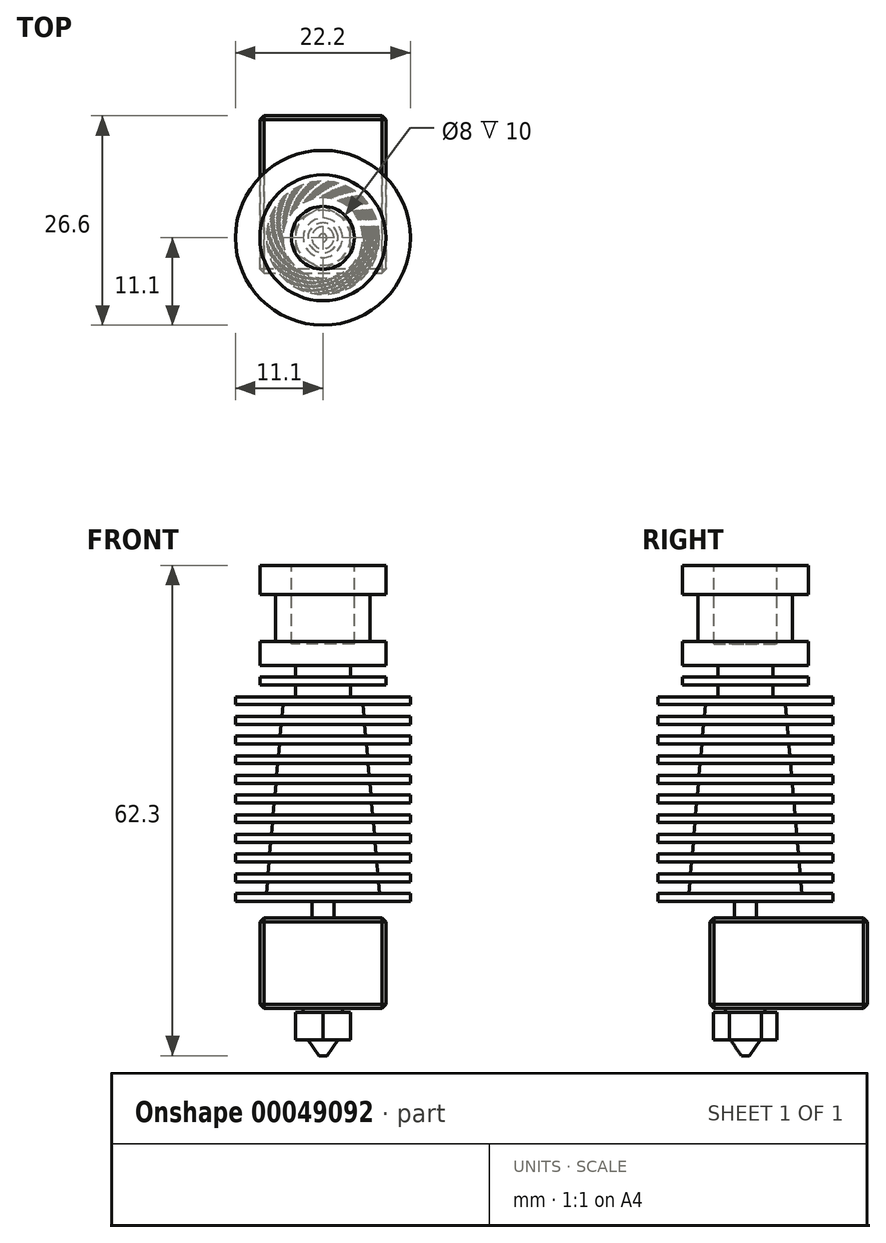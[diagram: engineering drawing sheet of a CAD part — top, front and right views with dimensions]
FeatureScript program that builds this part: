
annotation { "Feature Type Name" : "Feature", "Feature Type Description" : "" }
export const myFeature = defineFeature(function(context is Context, id is Id, definition is map)
    precondition{}
    {
        {
            var Q0;
            Q0=qCreatedBy(makeId("Front.planeOp"),FACE);
            var sketch = newSketch(context, id + "F0", { "sketchPlane" : qUnion([Q0])});
            skLineSegment(sketch, "E0", {"start": v(0, 42.7) * mm, "end": v(8, 42.7) * mm});
            skLineSegment(sketch, "E1", {"start": v(8, 42.7) * mm, "end": v(8, 39) * mm});
            skLineSegment(sketch, "E2", {"start": v(8, 39) * mm, "end": v(6, 39) * mm});
            skLineSegment(sketch, "E3", {"start": v(6, 39) * mm, "end": v(6, 33) * mm});
            skLineSegment(sketch, "E4", {"start": v(6, 33) * mm, "end": v(8, 33) * mm});
            skLineSegment(sketch, "E5", {"start": v(8, 33) * mm, "end": v(8, 30) * mm});
            skLineSegment(sketch, "E6", {"start": v(8, 30) * mm, "end": v(3.5, 30) * mm});
            skLineSegment(sketch, "E7", {"start": v(3.5, 30) * mm, "end": v(3.5, 28.5) * mm});
            skLineSegment(sketch, "E8", {"start": v(3.5, 28.5) * mm, "end": v(8, 28.5) * mm});
            skLineSegment(sketch, "E9", {"start": v(8, 28.5) * mm, "end": v(8, 27.5) * mm});
            skLineSegment(sketch, "E10", {"start": v(8, 27.5) * mm, "end": v(3.5, 27.5) * mm});
            skLineSegment(sketch, "E11", {"start": v(3.5, 27.5) * mm, "end": v(3.5, 26) * mm});
            skLineSegment(sketch, "E12", {"start": v(3.5, 26) * mm, "end": v(11.1, 26) * mm});
            skLineSegment(sketch, "E13", {"start": v(11.1, 26) * mm, "end": v(11.1, 0) * mm, "construction": true});
            skLineSegment(sketch, "E14", {"start": v(0, 0) * mm, "end": v(0, 42.7) * mm});
            skLineSegment(sketch, "E15", {"start": v(11.1, 0) * mm, "end": v(1.4, 0) * mm});
            skLineSegment(sketch, "E16", {"start": v(1.4, 0) * mm, "end": v(1.4, -2.1) * mm});
            skLineSegment(sketch, "E17", {"start": v(1.4, -2.1) * mm, "end": v(0, -2.1) * mm});
            skLineSegment(sketch, "E18", {"start": v(0, -2.1) * mm, "end": v(0, 0) * mm});
            skLineSegment(sketch, "E19", {"start": v(5, 26) * mm, "end": v(7.27, 0) * mm, "construction": true});
            skLineSegment(sketch, "E20", {"start": v(11.1, 26) * mm, "end": v(11.1, 25) * mm});
            skLineSegment(sketch, "E21", {"start": v(11.1, 25) * mm, "end": v(5.09, 25) * mm});
            skLineSegment(sketch, "E22", {"start": v(5.09, 25) * mm, "end": v(5.22, 23.5) * mm});
            skLineSegment(sketch, "E23", {"start": v(5.22, 23.5) * mm, "end": v(11.1, 23.5) * mm});
            skLineSegment(sketch, "E24", {"start": v(11.1, 23.5) * mm, "end": v(11.1, 22.5) * mm});
            skLineSegment(sketch, "E25", {"start": v(11.1, 22.5) * mm, "end": v(5.3, 22.5) * mm});
            skLineSegment(sketch, "E26", {"start": v(5.3, 22.5) * mm, "end": v(5.44, 21) * mm});
            skLineSegment(sketch, "E27", {"start": v(5.44, 21) * mm, "end": v(11.1, 21) * mm});
            skLineSegment(sketch, "E28", {"start": v(11.1, 21) * mm, "end": v(11.1, 20) * mm});
            skLineSegment(sketch, "E29", {"start": v(11.1, 20) * mm, "end": v(5.52, 20) * mm});
            skLineSegment(sketch, "E30", {"start": v(5.52, 20) * mm, "end": v(5.66, 18.5) * mm});
            skLineSegment(sketch, "E31", {"start": v(5.66, 18.5) * mm, "end": v(11.1, 18.5) * mm});
            skLineSegment(sketch, "E32", {"start": v(11.1, 18.5) * mm, "end": v(11.1, 17.5) * mm});
            skLineSegment(sketch, "E33", {"start": v(11.1, 17.5) * mm, "end": v(5.74, 17.5) * mm});
            skLineSegment(sketch, "E34", {"start": v(5.74, 17.5) * mm, "end": v(5.87, 16) * mm});
            skLineSegment(sketch, "E35", {"start": v(5.87, 16) * mm, "end": v(11.1, 16) * mm});
            skLineSegment(sketch, "E36", {"start": v(11.1, 16) * mm, "end": v(11.1, 15) * mm});
            skLineSegment(sketch, "E37", {"start": v(11.1, 15) * mm, "end": v(5.96, 15) * mm});
            skLineSegment(sketch, "E38", {"start": v(5.96, 15) * mm, "end": v(6.1, 13.5) * mm});
            skLineSegment(sketch, "E39", {"start": v(6.1, 13.5) * mm, "end": v(11.1, 13.5) * mm});
            skLineSegment(sketch, "E40", {"start": v(11.1, 13.5) * mm, "end": v(11.1, 12.5) * mm});
            skLineSegment(sketch, "E41", {"start": v(11.1, 12.5) * mm, "end": v(6.18, 12.5) * mm});
            skLineSegment(sketch, "E42", {"start": v(6.18, 12.5) * mm, "end": v(6.31, 11) * mm});
            skLineSegment(sketch, "E43", {"start": v(6.31, 11) * mm, "end": v(11.1, 11) * mm});
            skLineSegment(sketch, "E44", {"start": v(11.1, 11) * mm, "end": v(11.1, 10) * mm});
            skLineSegment(sketch, "E45", {"start": v(11.1, 10) * mm, "end": v(6.4, 10) * mm});
            skLineSegment(sketch, "E46", {"start": v(6.4, 10) * mm, "end": v(6.53, 8.5) * mm});
            skLineSegment(sketch, "E47", {"start": v(6.53, 8.5) * mm, "end": v(11.1, 8.5) * mm});
            skLineSegment(sketch, "E48", {"start": v(11.1, 8.5) * mm, "end": v(11.1, 7.5) * mm});
            skLineSegment(sketch, "E49", {"start": v(11.1, 7.5) * mm, "end": v(6.62, 7.5) * mm});
            skLineSegment(sketch, "E50", {"start": v(6.62, 7.5) * mm, "end": v(6.75, 6) * mm});
            skLineSegment(sketch, "E51", {"start": v(6.75, 6) * mm, "end": v(11.1, 6) * mm});
            skLineSegment(sketch, "E52", {"start": v(11.1, 6) * mm, "end": v(11.1, 5) * mm});
            skLineSegment(sketch, "E53", {"start": v(11.1, 5) * mm, "end": v(6.84, 5) * mm});
            skLineSegment(sketch, "E54", {"start": v(6.84, 5) * mm, "end": v(6.97, 3.5) * mm});
            skLineSegment(sketch, "E55", {"start": v(6.97, 3.5) * mm, "end": v(11.1, 3.5) * mm});
            skLineSegment(sketch, "E56", {"start": v(11.1, 3.5) * mm, "end": v(11.1, 2.5) * mm});
            skLineSegment(sketch, "E57", {"start": v(11.1, 2.5) * mm, "end": v(7.06, 2.5) * mm});
            skLineSegment(sketch, "E58", {"start": v(7.06, 2.5) * mm, "end": v(7.19, 1) * mm});
            skLineSegment(sketch, "E59", {"start": v(7.19, 1) * mm, "end": v(11.1, 1) * mm});
            skLineSegment(sketch, "E60", {"start": v(11.1, 1) * mm, "end": v(11.1, 0) * mm});
            skSolve(sketch);
        }
        {
            var Q0;
            Q0=makeQuery(id+"F0.imprint","IMPRINT",FACE,{"disambiguationData":[TD([[makeQuery(id+"F0.imprint","IMPRINT",EDGE,{"derivedFrom":sQuery(id+"F0.wireOp",EDGE,"E0")}),-1.0]])]});
            var Q1;
            Q1=sQuery(id+"F0.wireOp",EDGE,"E14");
            revolve(context, id + "F1", {"entities" : qUnion([Q0]), "axis" : qUnion([Q1]), "revolveType" : RevolveType.FULL});
        }
        {
            var Q0;
            Q0=makeQuery(id+"F1.opRevolve","SWEPT_FACE",FACE,{"disambiguationData":[OSD([sQuery(id+"F0.wireOp",EDGE,"E17")])]});
            var sketch = newSketch(context, id + "F2", { "sketchPlane" : qUnion([Q0])});
            skLineSegment(sketch, "E61.bottom", {"start": v(-15.5, 8) * mm, "end": v(4.5, 8) * mm});
            skLineSegment(sketch, "E61.top", {"start": v(-15.5, -8) * mm, "end": v(4.5, -8) * mm});
            skLineSegment(sketch, "E61.left", {"start": v(-15.5, 8) * mm, "end": v(-15.5, -8) * mm});
            skLineSegment(sketch, "E61.right", {"start": v(4.5, 8) * mm, "end": v(4.5, -8) * mm});
            skPoint(sketch, "E62.0", {"position": v(0, 0) * mm});
            skLineSegment(sketch, "E63", {"start": v(-15.5, 0) * mm, "end": v(4.5, 0) * mm, "construction": true});
            skSolve(sketch);
        }
        {
            var Q0;
            Q0=makeQuery(id+"F2.imprint","IMPRINT",FACE,{"disambiguationData":[TD([[makeQuery(id+"F2.imprint","IMPRINT",EDGE,{"derivedFrom":sQuery(id+"F2.wireOp",EDGE,"E61.bottom")}),-1.0]])]});
            var Q1;
            Q1=makeQuery(id+"F2.imprint","IMPRINT",FACE,{"disambiguationData":[TD([[makeQuery(id+"F2.imprint","IMPRINT",EDGE,{"derivedFrom":makeQuery(id+"F1.opRevolve","SWEPT_EDGE",EDGE,{"disambiguationData":[OSD([sQuery(id+"F0.wireOp",EDGE,"E16"),sQuery(id+"F0.wireOp",EDGE,"E17")])]})}),1.0]])]});
            extrude(context, id + "F3", {"entities" : qUnion([Q0, Q1]), "operationType" : NewBodyOperationType.ADD, "depth" : 11.5 * mm});
        }
        {
            var Q0;
            Q0=makeQuery(id+"F3.opExtrude","SWEPT_FACE",FACE,{"disambiguationData":[OSD([sQuery(id+"F2.wireOp",EDGE,"E61.bottom")])]});
            var Q1;
            Q1=makeQuery(id+"F3.opExtrude","SWEPT_FACE",FACE,{"disambiguationData":[OSD([sQuery(id+"F2.wireOp",EDGE,"E61.right")])]});
            var Q2;
            Q2=makeQuery(id+"F3.opExtrude","SWEPT_FACE",FACE,{"disambiguationData":[OSD([sQuery(id+"F2.wireOp",EDGE,"E61.top")])]});
            var Q3;
            Q3=makeQuery(id+"F3.opExtrude","SWEPT_FACE",FACE,{"disambiguationData":[OSD([sQuery(id+"F2.wireOp",EDGE,"E61.left")])]});
            chamfer(context, id + "F4", {"entities" : qUnion([Q0, Q1, Q2, Q3]), "width" : .5 * mm, "tangentPropagation" : true});
        }
        {
            var Q0;
            Q0=qCreatedBy(makeId("Front.planeOp"),FACE);
            var sketch = newSketch(context, id + "F5", { "sketchPlane" : qUnion([Q0])});
            skLineSegment(sketch, "E64", {"start": v(0, -7.1) * mm, "end": v(0, -19.6) * mm});
            skLineSegment(sketch, "E65", {"start": v(0, -19.6) * mm, "end": v(0.5, -19.6) * mm});
            skLineSegment(sketch, "E66", {"start": v(0.5, -19.6) * mm, "end": v(1.9, -17.6) * mm});
            skLineSegment(sketch, "E67", {"start": v(1.9, -17.6) * mm, "end": v(2.5, -17.6) * mm});
            skLineSegment(sketch, "E68", {"start": v(2.5, -17.6) * mm, "end": v(2.5, -14.6) * mm});
            skLineSegment(sketch, "E69", {"start": v(2.5, -14.6) * mm, "end": v(2.5, -7.1) * mm});
            skLineSegment(sketch, "E70", {"start": v(2.5, -7.1) * mm, "end": v(0, -7.1) * mm});
            skSolve(sketch);
        }
        {
            var Q0;
            Q0=makeQuery(id+"F5.imprint","IMPRINT",FACE,{"disambiguationData":[TD([[makeQuery(id+"F5.imprint","IMPRINT",EDGE,{"derivedFrom":sQuery(id+"F5.wireOp",EDGE,"E64")}),1.0]])]});
            var Q1;
            Q1=sQuery(id+"F5.wireOp",EDGE,"E64");
            revolve(context, id + "F6", {"operationType" : NewBodyOperationType.ADD, "entities" : qUnion([Q0]), "axis" : qUnion([Q1]), "revolveType" : RevolveType.FULL});
        }
        {
            var Q0;
            Q0=makeQuery(id+"F6.opRevolve","SWEPT_FACE",FACE,{"disambiguationData":[OSD([sQuery(id+"F5.wireOp",EDGE,"E67")])]});
            var sketch = newSketch(context, id + "F7", { "sketchPlane" : qUnion([Q0])});
            skCircle(sketch, "E71.cCircle", {"center": v(0, 0) * mm, "radius": 3.5 * mm, "construction": true});
            skLineSegment(sketch, "E71.0", {"start": v(4.04, 0) * mm, "end": v(2.02, -3.5) * mm});
            skLineSegment(sketch, "E71.1", {"start": v(2.02, -3.5) * mm, "end": v(-2.02, -3.5) * mm});
            skLineSegment(sketch, "E71.2", {"start": v(-2.02, -3.5) * mm, "end": v(-4.04, 0) * mm});
            skLineSegment(sketch, "E71.3", {"start": v(-4.04, 0) * mm, "end": v(-2.02, 3.5) * mm});
            skLineSegment(sketch, "E71.4", {"start": v(-2.02, 3.5) * mm, "end": v(2.02, 3.5) * mm});
            skLineSegment(sketch, "E71.5", {"start": v(2.02, 3.5) * mm, "end": v(4.04, 0) * mm});
            skPoint(sketch, "E71.0.midPoint", {"position": v(3.03, -1.75) * mm});
            skSolve(sketch);
        }
        {
            var Q0;
            Q0=makeQuery(id+"F7.imprint","IMPRINT",FACE,{"disambiguationData":[TD([[makeQuery(id+"F7.imprint","IMPRINT",EDGE,{"derivedFrom":sQuery(id+"F7.wireOp",EDGE,"E71.0")}),-1.0]])]});
            extrude(context, id + "F8", {"entities" : qUnion([Q0]), "operationType" : NewBodyOperationType.ADD, "oppositeDirection" : true, "depth" : 3.5 * mm});
        }
        {
            var Q0;
            Q0=makeQuery(id+"F1.opRevolve","SWEPT_BODY",BODY,{"disambiguationData":[OSD([sQuery(id+"F0.wireOp",EDGE,"E0"),sQuery(id+"F0.wireOp",EDGE,"E1"),sQuery(id+"F0.wireOp",EDGE,"E2"),sQuery(id+"F0.wireOp",EDGE,"E3"),sQuery(id+"F0.wireOp",EDGE,"E4"),sQuery(id+"F0.wireOp",EDGE,"E5"),sQuery(id+"F0.wireOp",EDGE,"E6"),sQuery(id+"F0.wireOp",EDGE,"E7"),sQuery(id+"F0.wireOp",EDGE,"E8"),sQuery(id+"F0.wireOp",EDGE,"E9"),sQuery(id+"F0.wireOp",EDGE,"E10"),sQuery(id+"F0.wireOp",EDGE,"E11"),sQuery(id+"F0.wireOp",EDGE,"E12"),sQuery(id+"F0.wireOp",EDGE,"E14"),sQuery(id+"F0.wireOp",EDGE,"E15"),sQuery(id+"F0.wireOp",EDGE,"E16"),sQuery(id+"F0.wireOp",EDGE,"E17"),sQuery(id+"F0.wireOp",EDGE,"E18"),sQuery(id+"F0.wireOp",EDGE,"E20"),sQuery(id+"F0.wireOp",EDGE,"E21"),sQuery(id+"F0.wireOp",EDGE,"E22"),sQuery(id+"F0.wireOp",EDGE,"E23"),sQuery(id+"F0.wireOp",EDGE,"E24"),sQuery(id+"F0.wireOp",EDGE,"E25"),sQuery(id+"F0.wireOp",EDGE,"E26"),sQuery(id+"F0.wireOp",EDGE,"E27"),sQuery(id+"F0.wireOp",EDGE,"E28"),sQuery(id+"F0.wireOp",EDGE,"E29"),sQuery(id+"F0.wireOp",EDGE,"E30"),sQuery(id+"F0.wireOp",EDGE,"E31"),sQuery(id+"F0.wireOp",EDGE,"E32"),sQuery(id+"F0.wireOp",EDGE,"E33"),sQuery(id+"F0.wireOp",EDGE,"E34"),sQuery(id+"F0.wireOp",EDGE,"E35"),sQuery(id+"F0.wireOp",EDGE,"E36"),sQuery(id+"F0.wireOp",EDGE,"E37"),sQuery(id+"F0.wireOp",EDGE,"E38"),sQuery(id+"F0.wireOp",EDGE,"E39"),sQuery(id+"F0.wireOp",EDGE,"E40"),sQuery(id+"F0.wireOp",EDGE,"E41"),sQuery(id+"F0.wireOp",EDGE,"E42"),sQuery(id+"F0.wireOp",EDGE,"E43"),sQuery(id+"F0.wireOp",EDGE,"E44"),sQuery(id+"F0.wireOp",EDGE,"E45"),sQuery(id+"F0.wireOp",EDGE,"E46"),sQuery(id+"F0.wireOp",EDGE,"E47"),sQuery(id+"F0.wireOp",EDGE,"E48"),sQuery(id+"F0.wireOp",EDGE,"E49"),sQuery(id+"F0.wireOp",EDGE,"E50"),sQuery(id+"F0.wireOp",EDGE,"E51"),sQuery(id+"F0.wireOp",EDGE,"E52"),sQuery(id+"F0.wireOp",EDGE,"E53"),sQuery(id+"F0.wireOp",EDGE,"E54"),sQuery(id+"F0.wireOp",EDGE,"E55"),sQuery(id+"F0.wireOp",EDGE,"E56"),sQuery(id+"F0.wireOp",EDGE,"E57"),sQuery(id+"F0.wireOp",EDGE,"E58"),sQuery(id+"F0.wireOp",EDGE,"E59"),sQuery(id+"F0.wireOp",EDGE,"E60")])]});
            var Q1;
            Q1=sQuery(id+"F0.wireOp",EDGE,"E14");
            transform(context, id + "F9", {"entities" : qUnion([Q0]), "transformType" : TransformType.ROTATION, "transformAxis" : qUnion([Q1]), "angle" : 90 * degree, "oppositeDirection" : true, "makeCopy" : false});
        }
        {
            var Q0;
            Q0=makeQuery(id+"F1.opRevolve","SWEPT_FACE",FACE,{"disambiguationData":[OSD([sQuery(id+"F0.wireOp",EDGE,"E0")])]});
            var sketch = newSketch(context, id + "F10", { "sketchPlane" : qUnion([Q0])});
            skCircle(sketch, "E72", {"center": v(0, 0) * mm, "radius": 4 * mm});
            skSolve(sketch);
        }
        {
            var Q0;
            Q0=makeQuery(id+"F10.imprint","IMPRINT",FACE,{"disambiguationData":[TD([[makeQuery(id+"F10.imprint","IMPRINT",EDGE,{"derivedFrom":sQuery(id+"F10.wireOp",EDGE,"E72")}),1.0]])]});
            extrude(context, id + "F11", {"entities" : qUnion([Q0]), "operationType" : NewBodyOperationType.REMOVE, "oppositeDirection" : true, "depth" : 10 * mm});
        }
    });
